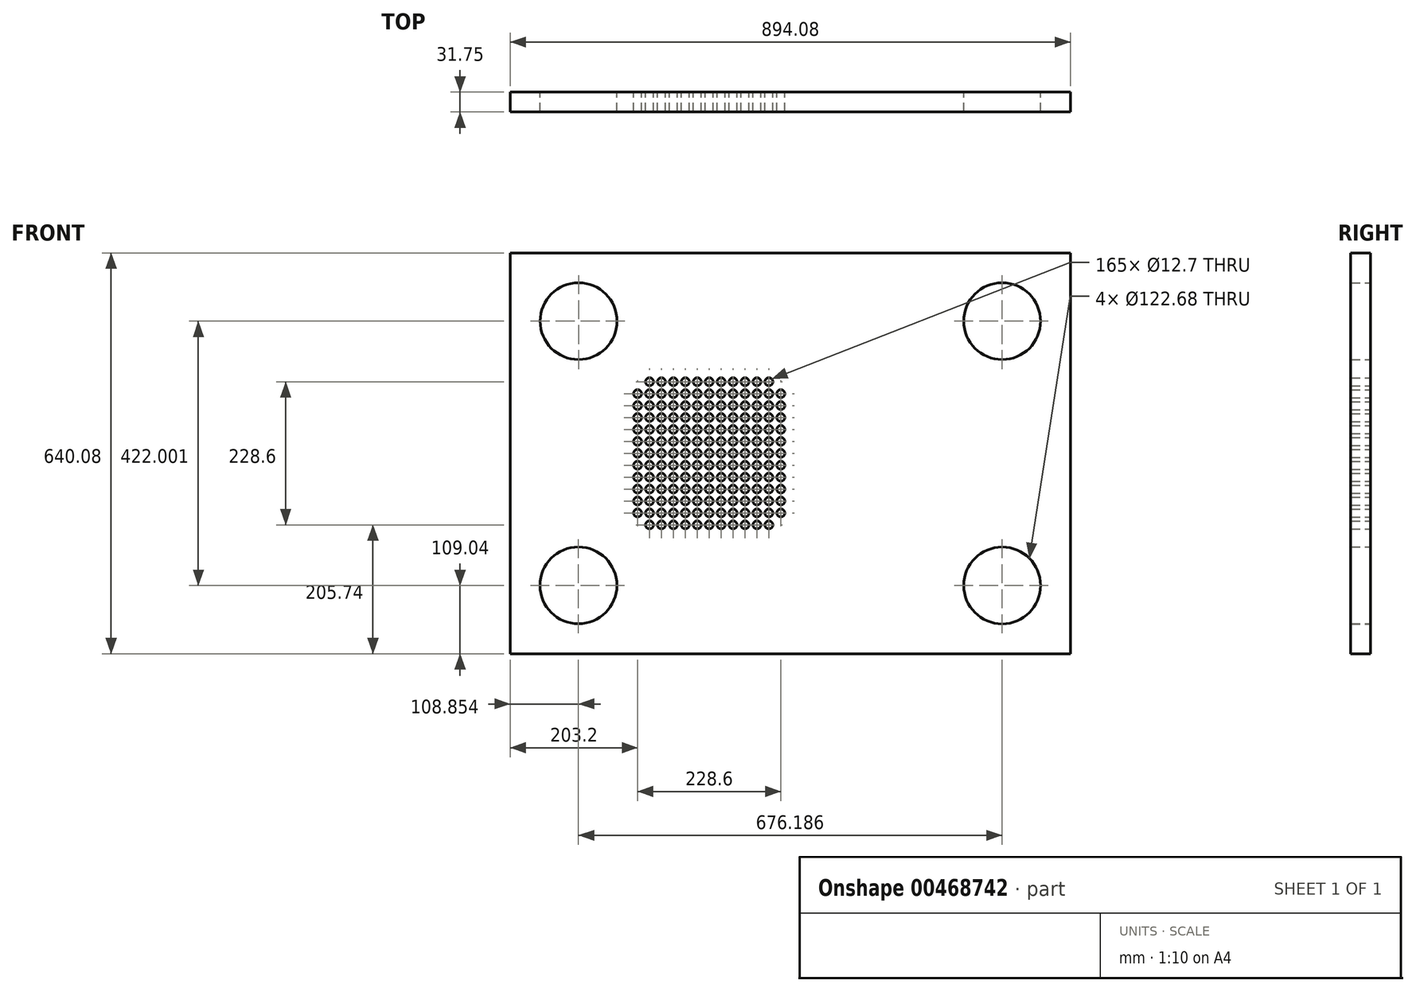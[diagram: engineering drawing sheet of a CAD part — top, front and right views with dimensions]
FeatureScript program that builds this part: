
annotation { "Feature Type Name" : "Feature", "Feature Type Description" : "" }
export const myFeature = defineFeature(function(context is Context, id is Id, definition is map)
    precondition{}
    {
        {
            var Q0;
            Q0=qCreatedBy(makeId("Front.planeOp"),FACE);
            var sketch = newSketch(context, id + "F0", { "sketchPlane" : qUnion([Q0])});
            skLineSegment(sketch, "E0", {"start": v(447.04, -320.04) * mm, "end": v(-447.04, -320.04) * mm});
            skLineSegment(sketch, "E1", {"start": v(-447.04, -320.04) * mm, "end": v(-447.04, 320.04) * mm});
            skCircle(sketch, "E2", {"center": v(-338, 211) * mm, "radius": 61.34 * mm});
            skCircle(sketch, "E3", {"center": v(338, 211) * mm, "radius": 61.34 * mm});
            skCircle(sketch, "E4", {"center": v(338, -211) * mm, "radius": 61.34 * mm});
            skCircle(sketch, "E5", {"center": v(-338.19, -210.81) * mm, "radius": 61.34 * mm});
            skLineSegment(sketch, "E6", {"start": v(-447.04, 320.04) * mm, "end": v(447.04, 320.04) * mm});
            skLineSegment(sketch, "E7", {"start": v(447.04, 320.04) * mm, "end": v(447.04, -320.04) * mm});
            skCircle(sketch, "E8", {"center": v(-243.84, 95.25) * mm, "radius": 6.35 * mm});
            skCircle(sketch, "E9", {"center": v(-243.84, 76.2) * mm, "radius": 6.35 * mm});
            skCircle(sketch, "E10", {"center": v(-243.84, 57.15) * mm, "radius": 6.35 * mm});
            skCircle(sketch, "E11", {"center": v(-243.84, 38.1) * mm, "radius": 6.35 * mm});
            skCircle(sketch, "E12", {"center": v(-224.79, 114.3) * mm, "radius": 6.35 * mm});
            skCircle(sketch, "E13", {"center": v(-224.79, 95.25) * mm, "radius": 6.35 * mm});
            skCircle(sketch, "E14", {"center": v(-224.79, 76.2) * mm, "radius": 6.35 * mm});
            skCircle(sketch, "E15", {"center": v(-224.79, 57.15) * mm, "radius": 6.35 * mm});
            skCircle(sketch, "E16", {"center": v(-224.79, 38.1) * mm, "radius": 6.35 * mm});
            skCircle(sketch, "E17", {"center": v(-205.74, 114.3) * mm, "radius": 6.35 * mm});
            skCircle(sketch, "E18", {"center": v(-205.74, 95.25) * mm, "radius": 6.35 * mm});
            skCircle(sketch, "E19", {"center": v(-205.74, 76.2) * mm, "radius": 6.35 * mm});
            skCircle(sketch, "E20", {"center": v(-205.74, 57.15) * mm, "radius": 6.35 * mm});
            skCircle(sketch, "E21", {"center": v(-205.74, 38.1) * mm, "radius": 6.35 * mm});
            skCircle(sketch, "E22", {"center": v(-186.69, 114.3) * mm, "radius": 6.35 * mm});
            skCircle(sketch, "E23", {"center": v(-186.69, 95.25) * mm, "radius": 6.35 * mm});
            skCircle(sketch, "E24", {"center": v(-186.69, 76.2) * mm, "radius": 6.35 * mm});
            skCircle(sketch, "E25", {"center": v(-186.69, 57.15) * mm, "radius": 6.35 * mm});
            skCircle(sketch, "E26", {"center": v(-186.69, 38.1) * mm, "radius": 6.35 * mm});
            skCircle(sketch, "E27", {"center": v(-167.64, 114.3) * mm, "radius": 6.35 * mm});
            skCircle(sketch, "E28", {"center": v(-167.64, 95.25) * mm, "radius": 6.35 * mm});
            skCircle(sketch, "E29", {"center": v(-167.64, 76.2) * mm, "radius": 6.35 * mm});
            skCircle(sketch, "E30", {"center": v(-167.64, 57.15) * mm, "radius": 6.35 * mm});
            skCircle(sketch, "E31", {"center": v(-167.64, 38.1) * mm, "radius": 6.35 * mm});
            skCircle(sketch, "E32", {"center": v(-148.59, 114.3) * mm, "radius": 6.35 * mm});
            skCircle(sketch, "E33", {"center": v(-148.59, 95.25) * mm, "radius": 6.35 * mm});
            skCircle(sketch, "E34", {"center": v(-148.59, 76.2) * mm, "radius": 6.35 * mm});
            skCircle(sketch, "E35", {"center": v(-148.59, 57.15) * mm, "radius": 6.35 * mm});
            skCircle(sketch, "E36", {"center": v(-148.59, 38.1) * mm, "radius": 6.35 * mm});
            skCircle(sketch, "E37", {"center": v(-129.54, 114.3) * mm, "radius": 6.35 * mm});
            skCircle(sketch, "E38", {"center": v(-129.54, 95.25) * mm, "radius": 6.35 * mm});
            skCircle(sketch, "E39", {"center": v(-129.54, 76.2) * mm, "radius": 6.35 * mm});
            skCircle(sketch, "E40", {"center": v(-129.54, 57.15) * mm, "radius": 6.35 * mm});
            skCircle(sketch, "E41", {"center": v(-129.54, 38.1) * mm, "radius": 6.35 * mm});
            skCircle(sketch, "E42", {"center": v(-243.84, 19.05) * mm, "radius": 6.35 * mm});
            skCircle(sketch, "E43", {"center": v(-243.84, 0) * mm, "radius": 6.35 * mm});
            skCircle(sketch, "E44", {"center": v(-243.84, -19.05) * mm, "radius": 6.35 * mm});
            skCircle(sketch, "E45", {"center": v(-243.84, -38.1) * mm, "radius": 6.35 * mm});
            skCircle(sketch, "E46", {"center": v(-224.79, 19.05) * mm, "radius": 6.35 * mm});
            skCircle(sketch, "E47", {"center": v(-224.79, 0) * mm, "radius": 6.35 * mm});
            skCircle(sketch, "E48", {"center": v(-224.79, -19.05) * mm, "radius": 6.35 * mm});
            skCircle(sketch, "E49", {"center": v(-224.79, -38.1) * mm, "radius": 6.35 * mm});
            skCircle(sketch, "E50", {"center": v(-205.74, 19.05) * mm, "radius": 6.35 * mm});
            skCircle(sketch, "E51", {"center": v(-205.74, 0) * mm, "radius": 6.35 * mm});
            skCircle(sketch, "E52", {"center": v(-205.74, -19.05) * mm, "radius": 6.35 * mm});
            skCircle(sketch, "E53", {"center": v(-205.74, -38.1) * mm, "radius": 6.35 * mm});
            skCircle(sketch, "E54", {"center": v(-186.69, 19.05) * mm, "radius": 6.35 * mm});
            skCircle(sketch, "E55", {"center": v(-186.69, 0) * mm, "radius": 6.35 * mm});
            skCircle(sketch, "E56", {"center": v(-186.69, -19.05) * mm, "radius": 6.35 * mm});
            skCircle(sketch, "E57", {"center": v(-186.69, -38.1) * mm, "radius": 6.35 * mm});
            skCircle(sketch, "E58", {"center": v(-167.64, 19.05) * mm, "radius": 6.35 * mm});
            skCircle(sketch, "E59", {"center": v(-167.64, 0) * mm, "radius": 6.35 * mm});
            skCircle(sketch, "E60", {"center": v(-167.64, -19.05) * mm, "radius": 6.35 * mm});
            skCircle(sketch, "E61", {"center": v(-167.64, -38.1) * mm, "radius": 6.35 * mm});
            skCircle(sketch, "E62", {"center": v(-148.59, 19.05) * mm, "radius": 6.35 * mm});
            skCircle(sketch, "E63", {"center": v(-148.59, 0) * mm, "radius": 6.35 * mm});
            skCircle(sketch, "E64", {"center": v(-148.59, -19.05) * mm, "radius": 6.35 * mm});
            skCircle(sketch, "E65", {"center": v(-148.59, -38.1) * mm, "radius": 6.35 * mm});
            skCircle(sketch, "E66", {"center": v(-129.54, 19.05) * mm, "radius": 6.35 * mm});
            skCircle(sketch, "E67", {"center": v(-129.54, 0) * mm, "radius": 6.35 * mm});
            skCircle(sketch, "E68", {"center": v(-129.54, -19.05) * mm, "radius": 6.35 * mm});
            skCircle(sketch, "E69", {"center": v(-129.54, -38.1) * mm, "radius": 6.35 * mm});
            skCircle(sketch, "E70", {"center": v(-110.49, 114.3) * mm, "radius": 6.35 * mm});
            skCircle(sketch, "E71", {"center": v(-110.49, 95.25) * mm, "radius": 6.35 * mm});
            skCircle(sketch, "E72", {"center": v(-110.49, 76.2) * mm, "radius": 6.35 * mm});
            skCircle(sketch, "E73", {"center": v(-110.49, 57.15) * mm, "radius": 6.35 * mm});
            skCircle(sketch, "E74", {"center": v(-110.49, 38.1) * mm, "radius": 6.35 * mm});
            skCircle(sketch, "E75", {"center": v(-91.44, 114.3) * mm, "radius": 6.35 * mm});
            skCircle(sketch, "E76", {"center": v(-91.44, 95.25) * mm, "radius": 6.35 * mm});
            skCircle(sketch, "E77", {"center": v(-91.44, 76.2) * mm, "radius": 6.35 * mm});
            skCircle(sketch, "E78", {"center": v(-91.44, 57.15) * mm, "radius": 6.35 * mm});
            skCircle(sketch, "E79", {"center": v(-91.44, 38.1) * mm, "radius": 6.35 * mm});
            skCircle(sketch, "E80", {"center": v(-72.39, 114.3) * mm, "radius": 6.35 * mm});
            skCircle(sketch, "E81", {"center": v(-72.39, 95.25) * mm, "radius": 6.35 * mm});
            skCircle(sketch, "E82", {"center": v(-72.39, 76.2) * mm, "radius": 6.35 * mm});
            skCircle(sketch, "E83", {"center": v(-72.39, 57.15) * mm, "radius": 6.35 * mm});
            skCircle(sketch, "E84", {"center": v(-72.39, 38.1) * mm, "radius": 6.35 * mm});
            skCircle(sketch, "E85", {"center": v(-53.34, 114.3) * mm, "radius": 6.35 * mm});
            skCircle(sketch, "E86", {"center": v(-53.34, 95.25) * mm, "radius": 6.35 * mm});
            skCircle(sketch, "E87", {"center": v(-53.34, 76.2) * mm, "radius": 6.35 * mm});
            skCircle(sketch, "E88", {"center": v(-53.34, 57.15) * mm, "radius": 6.35 * mm});
            skCircle(sketch, "E89", {"center": v(-53.34, 38.1) * mm, "radius": 6.35 * mm});
            skCircle(sketch, "E90", {"center": v(-34.29, 114.3) * mm, "radius": 6.35 * mm});
            skCircle(sketch, "E91", {"center": v(-34.29, 95.25) * mm, "radius": 6.35 * mm});
            skCircle(sketch, "E92", {"center": v(-34.29, 76.2) * mm, "radius": 6.35 * mm});
            skCircle(sketch, "E93", {"center": v(-34.29, 57.15) * mm, "radius": 6.35 * mm});
            skCircle(sketch, "E94", {"center": v(-34.29, 38.1) * mm, "radius": 6.35 * mm});
            skCircle(sketch, "E95", {"center": v(-15.24, 95.25) * mm, "radius": 6.35 * mm});
            skCircle(sketch, "E96", {"center": v(-15.24, 76.2) * mm, "radius": 6.35 * mm});
            skCircle(sketch, "E97", {"center": v(-15.24, 57.15) * mm, "radius": 6.35 * mm});
            skCircle(sketch, "E98", {"center": v(-15.24, 38.1) * mm, "radius": 6.35 * mm});
            skCircle(sketch, "E99", {"center": v(-110.49, 19.05) * mm, "radius": 6.35 * mm});
            skCircle(sketch, "E100", {"center": v(-110.49, 0) * mm, "radius": 6.35 * mm});
            skCircle(sketch, "E101", {"center": v(-110.49, -19.05) * mm, "radius": 6.35 * mm});
            skCircle(sketch, "E102", {"center": v(-110.49, -38.1) * mm, "radius": 6.35 * mm});
            skCircle(sketch, "E103", {"center": v(-91.44, 19.05) * mm, "radius": 6.35 * mm});
            skCircle(sketch, "E104", {"center": v(-91.44, 0) * mm, "radius": 6.35 * mm});
            skCircle(sketch, "E105", {"center": v(-91.44, -19.05) * mm, "radius": 6.35 * mm});
            skCircle(sketch, "E106", {"center": v(-91.44, -38.1) * mm, "radius": 6.35 * mm});
            skCircle(sketch, "E107", {"center": v(-72.39, 19.05) * mm, "radius": 6.35 * mm});
            skCircle(sketch, "E108", {"center": v(-72.39, 0) * mm, "radius": 6.35 * mm});
            skCircle(sketch, "E109", {"center": v(-72.39, -19.05) * mm, "radius": 6.35 * mm});
            skCircle(sketch, "E110", {"center": v(-72.39, -38.1) * mm, "radius": 6.35 * mm});
            skCircle(sketch, "E111", {"center": v(-53.34, 19.05) * mm, "radius": 6.35 * mm});
            skCircle(sketch, "E112", {"center": v(-53.34, 0) * mm, "radius": 6.35 * mm});
            skCircle(sketch, "E113", {"center": v(-53.34, -19.05) * mm, "radius": 6.35 * mm});
            skCircle(sketch, "E114", {"center": v(-53.34, -38.1) * mm, "radius": 6.35 * mm});
            skCircle(sketch, "E115", {"center": v(-34.29, 19.05) * mm, "radius": 6.35 * mm});
            skCircle(sketch, "E116", {"center": v(-34.29, 0) * mm, "radius": 6.35 * mm});
            skCircle(sketch, "E117", {"center": v(-34.29, -19.05) * mm, "radius": 6.35 * mm});
            skCircle(sketch, "E118", {"center": v(-34.29, -38.1) * mm, "radius": 6.35 * mm});
            skCircle(sketch, "E119", {"center": v(-15.24, 19.05) * mm, "radius": 6.35 * mm});
            skCircle(sketch, "E120", {"center": v(-15.24, 0) * mm, "radius": 6.35 * mm});
            skCircle(sketch, "E121", {"center": v(-15.24, -19.05) * mm, "radius": 6.35 * mm});
            skCircle(sketch, "E122", {"center": v(-15.24, -38.1) * mm, "radius": 6.35 * mm});
            skCircle(sketch, "E123", {"center": v(-243.84, -57.15) * mm, "radius": 6.35 * mm});
            skCircle(sketch, "E124", {"center": v(-243.84, -76.2) * mm, "radius": 6.35 * mm});
            skCircle(sketch, "E125", {"center": v(-243.84, -95.25) * mm, "radius": 6.35 * mm});
            skCircle(sketch, "E126", {"center": v(-224.79, -57.15) * mm, "radius": 6.35 * mm});
            skCircle(sketch, "E127", {"center": v(-224.79, -76.2) * mm, "radius": 6.35 * mm});
            skCircle(sketch, "E128", {"center": v(-224.79, -95.25) * mm, "radius": 6.35 * mm});
            skCircle(sketch, "E129", {"center": v(-224.79, -114.3) * mm, "radius": 6.35 * mm});
            skCircle(sketch, "E130", {"center": v(-205.74, -57.15) * mm, "radius": 6.35 * mm});
            skCircle(sketch, "E131", {"center": v(-205.74, -76.2) * mm, "radius": 6.35 * mm});
            skCircle(sketch, "E132", {"center": v(-205.74, -95.25) * mm, "radius": 6.35 * mm});
            skCircle(sketch, "E133", {"center": v(-205.74, -114.3) * mm, "radius": 6.35 * mm});
            skCircle(sketch, "E134", {"center": v(-186.69, -57.15) * mm, "radius": 6.35 * mm});
            skCircle(sketch, "E135", {"center": v(-186.69, -76.2) * mm, "radius": 6.35 * mm});
            skCircle(sketch, "E136", {"center": v(-186.69, -95.25) * mm, "radius": 6.35 * mm});
            skCircle(sketch, "E137", {"center": v(-186.69, -114.3) * mm, "radius": 6.35 * mm});
            skCircle(sketch, "E138", {"center": v(-167.64, -57.15) * mm, "radius": 6.35 * mm});
            skCircle(sketch, "E139", {"center": v(-167.64, -76.2) * mm, "radius": 6.35 * mm});
            skCircle(sketch, "E140", {"center": v(-167.64, -95.25) * mm, "radius": 6.35 * mm});
            skCircle(sketch, "E141", {"center": v(-167.64, -114.3) * mm, "radius": 6.35 * mm});
            skCircle(sketch, "E142", {"center": v(-148.59, -57.15) * mm, "radius": 6.35 * mm});
            skCircle(sketch, "E143", {"center": v(-148.59, -76.2) * mm, "radius": 6.35 * mm});
            skCircle(sketch, "E144", {"center": v(-148.59, -95.25) * mm, "radius": 6.35 * mm});
            skCircle(sketch, "E145", {"center": v(-148.59, -114.3) * mm, "radius": 6.35 * mm});
            skCircle(sketch, "E146", {"center": v(-129.54, -57.15) * mm, "radius": 6.35 * mm});
            skCircle(sketch, "E147", {"center": v(-129.54, -76.2) * mm, "radius": 6.35 * mm});
            skCircle(sketch, "E148", {"center": v(-129.54, -95.25) * mm, "radius": 6.35 * mm});
            skCircle(sketch, "E149", {"center": v(-129.54, -114.3) * mm, "radius": 6.35 * mm});
            skCircle(sketch, "E150", {"center": v(-110.49, -57.15) * mm, "radius": 6.35 * mm});
            skCircle(sketch, "E151", {"center": v(-110.49, -76.2) * mm, "radius": 6.35 * mm});
            skCircle(sketch, "E152", {"center": v(-110.49, -95.25) * mm, "radius": 6.35 * mm});
            skCircle(sketch, "E153", {"center": v(-110.49, -114.3) * mm, "radius": 6.35 * mm});
            skCircle(sketch, "E154", {"center": v(-91.44, -57.15) * mm, "radius": 6.35 * mm});
            skCircle(sketch, "E155", {"center": v(-91.44, -76.2) * mm, "radius": 6.35 * mm});
            skCircle(sketch, "E156", {"center": v(-91.44, -95.25) * mm, "radius": 6.35 * mm});
            skCircle(sketch, "E157", {"center": v(-91.44, -114.3) * mm, "radius": 6.35 * mm});
            skCircle(sketch, "E158", {"center": v(-72.39, -57.15) * mm, "radius": 6.35 * mm});
            skCircle(sketch, "E159", {"center": v(-72.39, -76.2) * mm, "radius": 6.35 * mm});
            skCircle(sketch, "E160", {"center": v(-72.39, -95.25) * mm, "radius": 6.35 * mm});
            skCircle(sketch, "E161", {"center": v(-72.39, -114.3) * mm, "radius": 6.35 * mm});
            skCircle(sketch, "E162", {"center": v(-53.34, -57.15) * mm, "radius": 6.35 * mm});
            skCircle(sketch, "E163", {"center": v(-53.34, -76.2) * mm, "radius": 6.35 * mm});
            skCircle(sketch, "E164", {"center": v(-53.34, -95.25) * mm, "radius": 6.35 * mm});
            skCircle(sketch, "E165", {"center": v(-53.34, -114.3) * mm, "radius": 6.35 * mm});
            skCircle(sketch, "E166", {"center": v(-34.29, -57.15) * mm, "radius": 6.35 * mm});
            skCircle(sketch, "E167", {"center": v(-34.29, -76.2) * mm, "radius": 6.35 * mm});
            skCircle(sketch, "E168", {"center": v(-34.29, -95.25) * mm, "radius": 6.35 * mm});
            skCircle(sketch, "E169", {"center": v(-34.29, -114.3) * mm, "radius": 6.35 * mm});
            skCircle(sketch, "E170", {"center": v(-15.24, -57.15) * mm, "radius": 6.35 * mm});
            skCircle(sketch, "E171", {"center": v(-15.24, -76.2) * mm, "radius": 6.35 * mm});
            skCircle(sketch, "E172", {"center": v(-15.24, -95.25) * mm, "radius": 6.35 * mm});
            skSolve(sketch);
        }
        {
            var Q0;
            Q0=makeQuery(id+"F0.imprint","IMPRINT",FACE,{"disambiguationData":[TD([[makeQuery(id+"F0.imprint","IMPRINT",EDGE,{"derivedFrom":sQuery(id+"F0.wireOp",EDGE,"E0")}),-1.0]])]});
            extrude(context, id + "F1", {"entities" : qUnion([Q0]), "depth" : 31.75 * mm});
        }
    });
